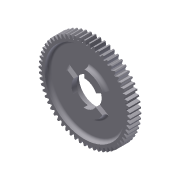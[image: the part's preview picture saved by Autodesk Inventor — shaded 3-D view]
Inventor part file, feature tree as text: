
AUTODESK INVENTOR PART (.ipt)
format: ipt  version: 2011 (Build 150239000, 239)  size: 479,744 bytes
history: native  units: mm (DEFAULTED — no unit token found)
features: sketch x6, other x4, extrude x4, plane x3, revolve x1, pattern_circular x1, fillet x1, projected_geometry x1
ambient origin geometry x8: Origin, YZ Plane, XZ Plane, XY Plane, X Axis, Y Axis, Z Axis, Center Point
bodies: Solid1 (feature_tree)
feature tree (21):
  other  "Gear 60T dog shift"
  extrude  "Extrusion1"  Depth=9.525mm TaperAngle=0.0deg
  plane  "Work Plane1"
  plane  "Work Plane2"
  plane  "Work Plane3"
  other  "Spur Gear"
  extrude  "Extrusion4"  Depth=76.2mm TaperAngle=0.0deg
  extrude  "Extrusion5"  TaperAngle=0.0deg  [1 undecoded]
  revolve  "Revolution2"  [1 undecoded]
  extrude  "Extrusion6"  Depth=28.575mm
  pattern_circular  "Circular Pattern1"  [2 undecoded]
  fillet  "Fillet1"  Radius=5.08mm
  sketch  "Sketch1"  dims[d0=78.74mm d1=9.525mm d2=0.0mm]
  sketch  "Sketch2"  dims[d3=76.2mm d4=76.2mm d5=0.0mm]
  other  "Srf1"
  sketch  "Sketch6"  dims[d6=0.0mm d7=0.523599mm d9=0.0mm]
  sketch  "Sketch7"  dims[d14=0.0mm d15=190.5mm d16=0.0mm]
  sketch  "Sketch8"  dims[d17=0.0mm d18=0.0mm d19=190.5mm d32=28.575mm]
  sketch  "Sketch9"  dims[d33=5.08mm d34=0.0mm d35=22.225mm d36=5.08mm d37=0.0mm d38=17.78mm d39=5.08mm d40=3.6576mm d41=90.0deg d42=9.773844mm d43=3.6576mm d44=0.0mm d45=30.0mm d46=360.0deg d48=2.54mm]
  other  "Pitch Diameter"
  projected_geometry  "Project Cut Edges1"
note: 4 required parameter values undecoded (feature->parameter linkage not recoverable at this tier; creation-order binding heuristic only, values carry confidence <= 0.55)